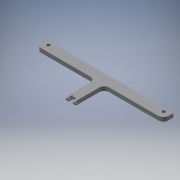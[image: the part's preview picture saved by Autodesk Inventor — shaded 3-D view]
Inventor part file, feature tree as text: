
AUTODESK INVENTOR PART (.ipt)
format: ipt  version: 2017 (Build 210142000, 142)  size: 147,456 bytes
history: native  units: mm
features: fillet x3, sketch x1, extrude x1, hole x1
ambient origin geometry x8: Origin, YZ Plane, XZ Plane, XY Plane, X Axis, Y Axis, Z Axis, Center Point
bodies: Solid1 (feature_tree)
feature tree (6):
  sketch  "Sketch1"  dims[d1=20.0mm d2=4.0mm d3=8.5mm d4=3.25mm d5=3.25mm d6=4.0mm d7=8.5mm d8=3.25mm d9=3.25mm d14=242.25mm d25=8.0mm d26=0.0mm d36=4.0mm d40=50.0mm d41=10.0mm d42=5.0mm d43=0.0mm d44=9.0mm d45=9.0mm d46=4.0mm d47=4.0mm d48=10.0mm d49=10.0mm d50=3.0mm d51=6.0mm d52=4.0mm d53=2.0mm d54=90.0deg d55=8.0mm d56=20.594885mm d67=10.0mm d68=3.0mm]
  extrude  "Extrusion1"  Depth=4.0mm
  fillet  "Fillet2"  Radius=8.5mm
  hole  "Hole1"  [1 undecoded]
  fillet  "Fillet5"  Radius=3.25mm
  fillet  "Fillet6"  Radius=4.0mm
note: 1 required parameter value undecoded (feature->parameter linkage not recoverable at this tier; creation-order binding heuristic only, values carry confidence <= 0.55)
